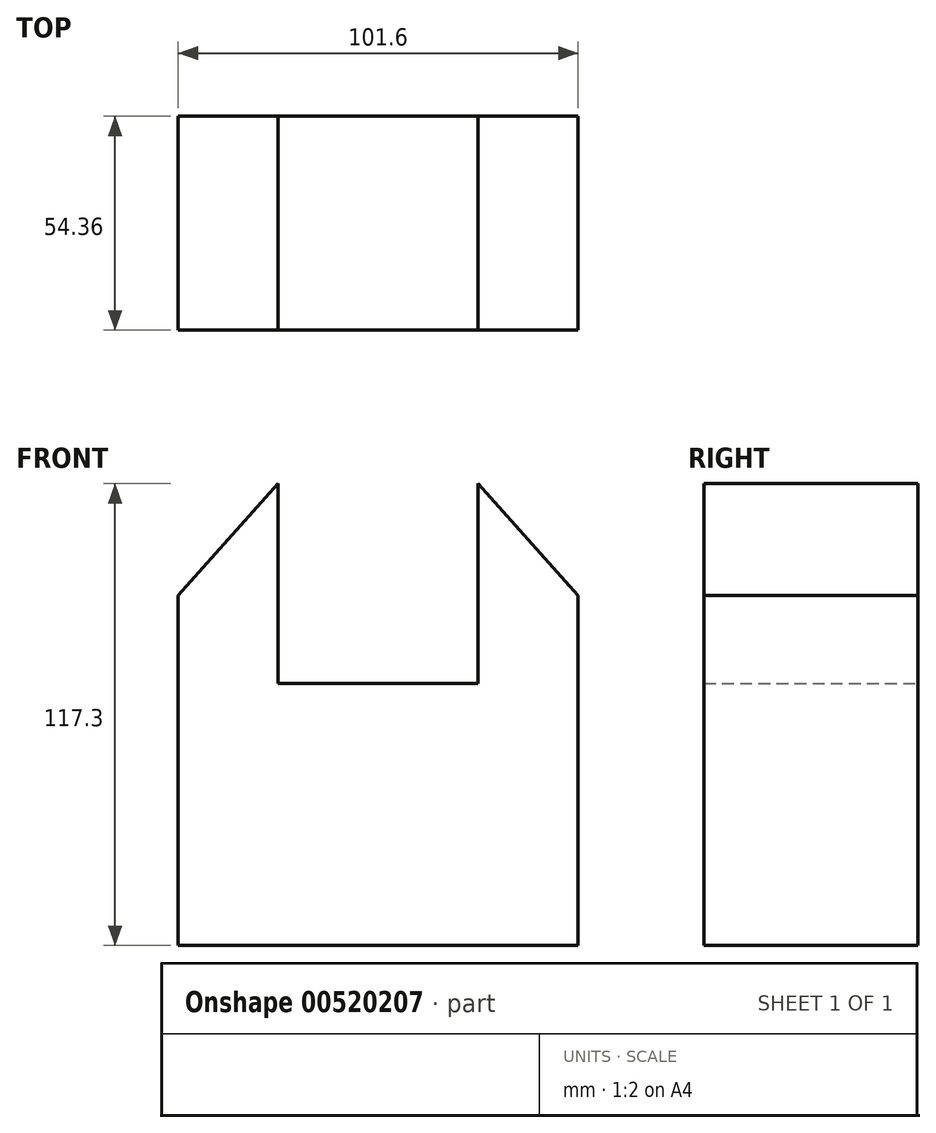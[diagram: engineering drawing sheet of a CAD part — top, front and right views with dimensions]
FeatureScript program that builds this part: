
annotation { "Feature Type Name" : "Feature", "Feature Type Description" : "" }
export const myFeature = defineFeature(function(context is Context, id is Id, definition is map)
    precondition{}
    {
        {
            var Q0;
            Q0=qCreatedBy(makeId("Front.planeOp"),FACE);
            var sketch = newSketch(context, id + "F0", { "sketchPlane" : qUnion([Q0])});
            skLineSegment(sketch, "E0.bottom", {"start": v(-41.25, 2.9) * mm, "end": v(-15.85, 2.9) * mm});
            skLineSegment(sketch, "E0.top", {"start": v(-41.25, -22.5) * mm, "end": v(-15.85, -22.5) * mm});
            skLineSegment(sketch, "E0.left", {"start": v(-41.25, 2.9) * mm, "end": v(-41.25, -22.5) * mm});
            skLineSegment(sketch, "E0.right", {"start": v(-15.85, 2.9) * mm, "end": v(-15.85, -22.5) * mm});
            skLineSegment(sketch, "E1.bottom", {"start": v(-15.85, 2.9) * mm, "end": v(34.95, 2.9) * mm});
            skLineSegment(sketch, "E1.top", {"start": v(-15.85, -22.5) * mm, "end": v(34.95, -22.5) * mm});
            skLineSegment(sketch, "E1.right", {"start": v(34.95, 2.9) * mm, "end": v(34.95, -22.5) * mm});
            skLineSegment(sketch, "E2.bottom", {"start": v(34.95, 2.9) * mm, "end": v(60.35, 2.9) * mm});
            skLineSegment(sketch, "E2.top", {"start": v(34.95, -22.5) * mm, "end": v(60.35, -22.5) * mm});
            skLineSegment(sketch, "E2.right", {"start": v(60.35, 2.9) * mm, "end": v(60.35, -22.5) * mm});
            skLineSegment(sketch, "E3.bottom", {"start": v(-41.25, 2.9) * mm, "end": v(-41.25, 2.9) * mm});
            skLineSegment(sketch, "E3.top", {"start": v(-41.25, 66.4) * mm, "end": v(-41.25, 66.4) * mm});
            skLineSegment(sketch, "E3.left", {"start": v(-41.25, 2.9) * mm, "end": v(-41.25, 66.4) * mm});
            skLineSegment(sketch, "E3.right", {"start": v(-41.25, 2.9) * mm, "end": v(-41.25, 66.4) * mm});
            skLineSegment(sketch, "E4", {"start": v(-41.25, 66.4) * mm, "end": v(-15.85, 94.8) * mm});
            skLineSegment(sketch, "E5.bottom", {"start": v(-15.85, 94.8) * mm, "end": v(-15.85, 94.8) * mm});
            skLineSegment(sketch, "E6", {"start": v(-15.85, 94.8) * mm, "end": v(-15.85, 44) * mm});
            skLineSegment(sketch, "E7", {"start": v(-15.85, 44) * mm, "end": v(34.95, 44) * mm});
            skLineSegment(sketch, "E8", {"start": v(34.95, 44) * mm, "end": v(34.95, 94.8) * mm});
            skLineSegment(sketch, "E9", {"start": v(60.35, 2.9) * mm, "end": v(60.35, 66.4) * mm});
            skLineSegment(sketch, "E10", {"start": v(60.35, 66.4) * mm, "end": v(34.95, 94.8) * mm});
            skSolve(sketch);
        }
        {
            var Q0;
            Q0=makeQuery(id+"F0.imprint","IMPRINT",FACE,{"disambiguationData":[TD([[makeQuery(id+"F0.imprint","IMPRINT",EDGE,{"derivedFrom":sQuery(id+"F0.wireOp",EDGE,"E0.bottom")}),-1.0]])]});
            var Q1;
            Q1=makeQuery(id+"F0.imprint","IMPRINT",FACE,{"disambiguationData":[TD([[makeQuery(id+"F0.imprint","IMPRINT",EDGE,{"derivedFrom":sQuery(id+"F0.wireOp",EDGE,"E1.bottom")}),-1.0]])]});
            var Q2;
            Q2=makeQuery(id+"F0.imprint","IMPRINT",FACE,{"disambiguationData":[TD([[makeQuery(id+"F0.imprint","IMPRINT",EDGE,{"derivedFrom":sQuery(id+"F0.wireOp",EDGE,"E2.bottom")}),-1.0]])]});
            var Q3;
            Q3=makeQuery(id+"F0.imprint","IMPRINT",FACE,{"disambiguationData":[TD([[makeQuery(id+"F0.imprint","IMPRINT",EDGE,{"derivedFrom":sQuery(id+"F0.wireOp",EDGE,"E0.bottom")}),1.0]])]});
            extrude(context, id + "F1", {"entities" : qUnion([Q0, Q1, Q2, Q3]), "depth" : 25.4 * mm, "offsetDistance" : 25.4 * mm});
        }
        {
            var Q0;
            Q0=makeQuery(id+"F1.opExtrude","CAP_FACE",FACE,{"disambiguationData":[OSD([sQuery(id+"F0.wireOp",EDGE,"E0.top"),sQuery(id+"F0.wireOp",EDGE,"E0.left"),sQuery(id+"F0.wireOp",EDGE,"E1.top"),sQuery(id+"F0.wireOp",EDGE,"E2.top"),sQuery(id+"F0.wireOp",EDGE,"E2.right"),sQuery(id+"F0.wireOp",EDGE,"E3.right"),sQuery(id+"F0.wireOp",EDGE,"E4"),sQuery(id+"F0.wireOp",EDGE,"E6"),sQuery(id+"F0.wireOp",EDGE,"E7"),sQuery(id+"F0.wireOp",EDGE,"E8"),sQuery(id+"F0.wireOp",EDGE,"E9"),sQuery(id+"F0.wireOp",EDGE,"E10")])],"isStart":false});
            extrude(context, id + "F2", {"entities" : qUnion([Q0]), "operationType" : NewBodyOperationType.ADD, "depth" : 28.96 * mm, "offsetDistance" : 25.4 * mm});
        }
    });
